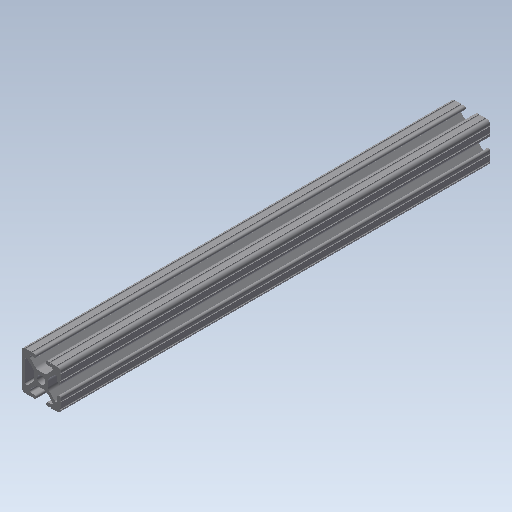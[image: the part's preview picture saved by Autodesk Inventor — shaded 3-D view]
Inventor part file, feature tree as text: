
AUTODESK INVENTOR PART (.ipt)
format: ipt  version: 2020 (Build 240168000, 168)  size: 220,672 bytes
history: native  units: in
note: dims shown in document units (in); Inventor stores cm internally (conversion verified against a paired STEP export)
features: extrude x1, sketch x1
ambient origin geometry x8: Origin, YZ Plane, XZ Plane, XY Plane, X Axis, Y Axis, Z Axis, Center Point
bodies: Solid1 (feature_tree)
feature tree (2):
  extrude  "Extrusion1"  [1 undecoded]
  sketch  "Sketch_1"  dims[d0=11.0in d1=0.0in]
note: 1 required parameter value undecoded (feature->parameter linkage not recoverable at this tier; creation-order binding heuristic only, values carry confidence <= 0.55)
